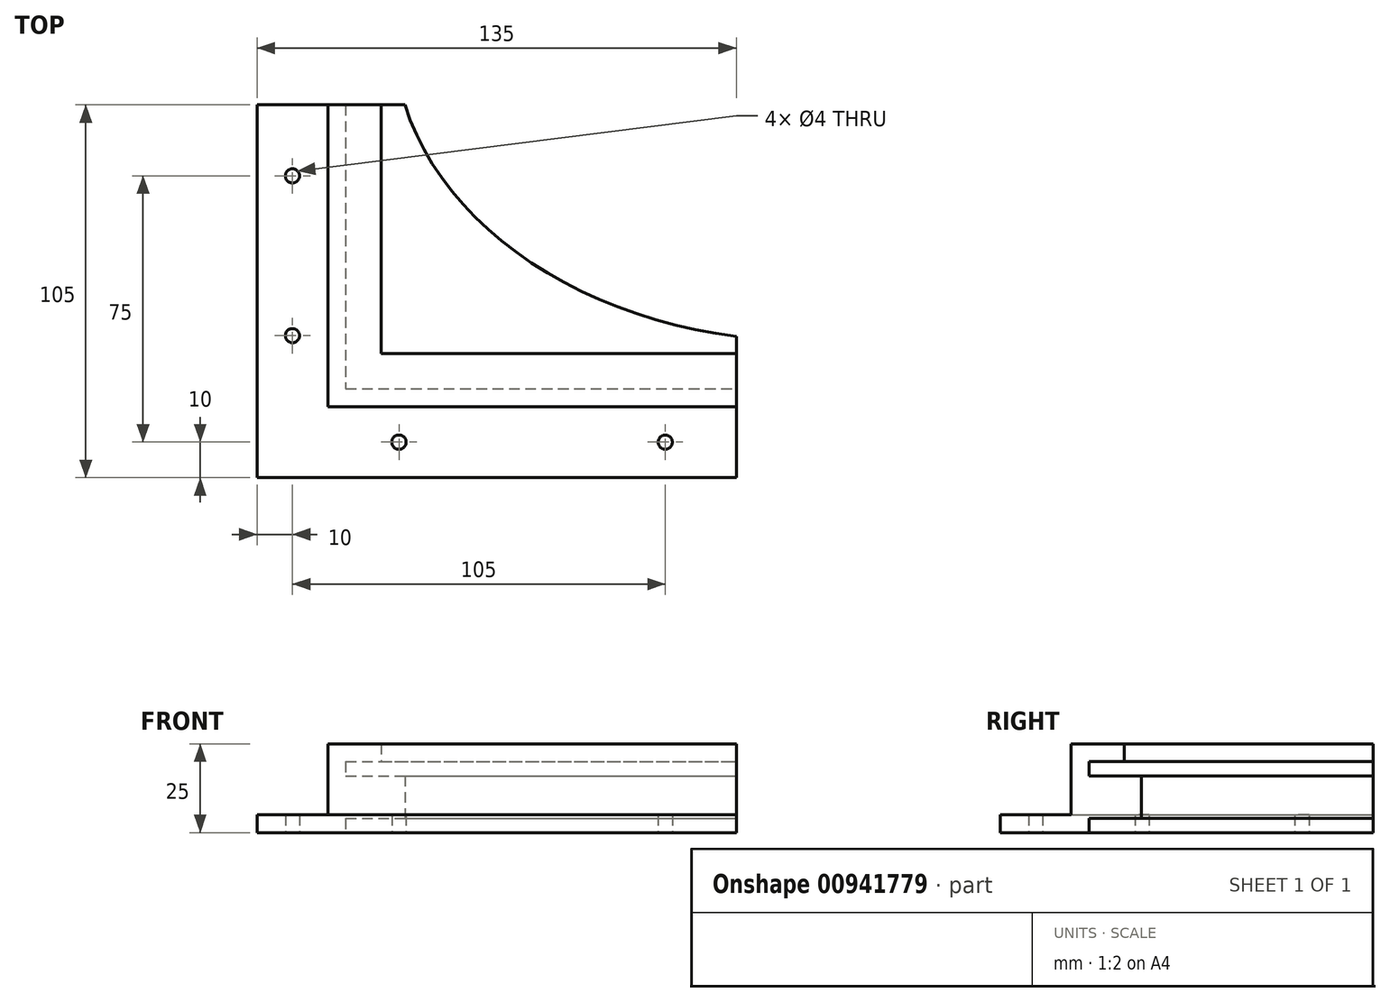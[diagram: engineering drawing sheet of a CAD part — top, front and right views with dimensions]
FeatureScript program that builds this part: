
annotation { "Feature Type Name" : "Feature", "Feature Type Description" : "" }
export const myFeature = defineFeature(function(context is Context, id is Id, definition is map)
    precondition{}
    {
        {
            var Q0;
            Q0=qCreatedBy(makeId("Top.planeOp"),FACE);
            var sketch = newSketch(context, id + "F0", { "sketchPlane" : qUnion([Q0])});
            skEllipticalArc(sketch, "E0", {});
            skLineSegment(sketch, "E1", {"start": v(-116.5, 0) * mm, "end": v(-116.5, -86.5) * mm});
            skPoint(sketch, "E1.endSnap0", {"position": v(0, -86.5) * mm});
            skLineSegment(sketch, "E2", {"start": v(-116.5, -86.5) * mm, "end": v(0, -86.5) * mm});
            skLineSegment(sketch, "E3", {"start": v(-116.5, 0) * mm, "end": v(-130, 0) * mm});
            skLineSegment(sketch, "E4", {"start": v(-130, 0) * mm, "end": v(-130, -100) * mm});
            skLineSegment(sketch, "E5", {"start": v(-130, -100) * mm, "end": v(0, -100) * mm});
            skLineSegment(sketch, "E6", {"start": v(0, -100) * mm, "end": v(0, -86.5) * mm});
            const initialGuessF0  = {"E0": [0, 0, 1, 0, 0.1165, 0.0865, 3.141592653589793, 4.71238898038469]};
            skSetInitialGuess(sketch, initialGuessF0);
            skSolve(sketch);
        }
        {
            var Q0;
            Q0=qSketchRegion(id+"F0",true);
            extrude(context, id + "F1", {"entities" : qUnion([Q0]), "depth" : 12 * mm, "offsetDistance" : 25 * mm});
        }
        {
            var Q0;
            Q0=makeQuery(id+"F1.opExtrude","SWEPT_FACE",FACE,{"disambiguationData":[OSD([sQuery(id+"F0.wireOp",EDGE,"E5")])]});
            var sketch = newSketch(context, id + "F2", { "sketchPlane" : qUnion([Q0])});
            skLineSegment(sketch, "E7.bottom", {"start": v(-130, 16) * mm, "end": v(0, 16) * mm});
            skLineSegment(sketch, "E7.top", {"start": v(-130, -4) * mm, "end": v(0, -4) * mm});
            skLineSegment(sketch, "E7.left", {"start": v(-130, 16) * mm, "end": v(-130, -4) * mm});
            skLineSegment(sketch, "E7.right", {"start": v(0, 16) * mm, "end": v(0, -4) * mm});
            skSolve(sketch);
        }
        {
            var Q0;
            Q0=qSketchRegion(id+"F2",true);
            extrude(context, id + "F3", {"entities" : qUnion([Q0]), "operationType" : NewBodyOperationType.ADD, "depth" : 5 * mm, "offsetDistance" : 25 * mm});
        }
        {
            var Q0;
            Q0=makeQuery(id+"F3.boolean.opBoolean","MERGE",FACE,{"derivedFrom":[makeQuery(id+"F1.opExtrude","SWEPT_FACE",FACE,{"disambiguationData":[OSD([sQuery(id+"F0.wireOp",EDGE,"E4")])]}),makeQuery(id+"F3.opExtrude","SWEPT_FACE",FACE,{"disambiguationData":[OSD([sQuery(id+"F2.wireOp",EDGE,"E7.left")])]})]});
            var sketch = newSketch(context, id + "F4", { "sketchPlane" : qUnion([Q0])});
            skLineSegment(sketch, "E8.bottom", {"start": v(105, 16) * mm, "end": v(0, 16) * mm});
            skLineSegment(sketch, "E8.top", {"start": v(105, -4) * mm, "end": v(0, -4) * mm});
            skLineSegment(sketch, "E8.left", {"start": v(105, 16) * mm, "end": v(105, -4) * mm});
            skLineSegment(sketch, "E8.right", {"start": v(0, 16) * mm, "end": v(0, -4) * mm});
            skSolve(sketch);
        }
        {
            var Q0;
            Q0=qSketchRegion(id+"F4",true);
            extrude(context, id + "F5", {"entities" : qUnion([Q0]), "operationType" : NewBodyOperationType.ADD, "depth" : 5 * mm, "offsetDistance" : 25 * mm});
        }
        {
            var Q0;
            Q0=makeQuery(id+"F5.boolean.opBoolean","MERGE",FACE,{"derivedFrom":[makeQuery(id+"F3.opExtrude","SWEPT_FACE",FACE,{"disambiguationData":[OSD([sQuery(id+"F2.wireOp",EDGE,"E7.top")])]}),makeQuery(id+"F5.opExtrude","SWEPT_FACE",FACE,{"disambiguationData":[OSD([sQuery(id+"F4.wireOp",EDGE,"E8.top")])]})]});
            var sketch = newSketch(context, id + "F6", { "sketchPlane" : qUnion([Q0])});
            skLineSegment(sketch, "E9", {"start": v(0, 125) * mm, "end": v(-155, 125) * mm});
            skLineSegment(sketch, "E10", {"start": v(-155, 125) * mm, "end": v(-155, 0) * mm});
            skLineSegment(sketch, "E11", {"start": v(-155, 0) * mm, "end": v(-135, 0) * mm});
            skLineSegment(sketch, "E12", {"start": v(-135, 0) * mm, "end": v(-135, 105) * mm});
            skLineSegment(sketch, "E13", {"start": v(-135, 105) * mm, "end": v(0, 105) * mm});
            skLineSegment(sketch, "E14", {"start": v(0, 105) * mm, "end": v(0, 125) * mm});
            skCircle(sketch, "E15", {"center": v(-145, 40) * mm, "radius": 2 * mm});
            skCircle(sketch, "E16", {"center": v(-145, 85) * mm, "radius": 2 * mm});
            skCircle(sketch, "E17", {"center": v(-115, 115) * mm, "radius": 2 * mm});
            skCircle(sketch, "E18", {"center": v(-40, 115) * mm, "radius": 2 * mm});
            skSolve(sketch);
        }
        {
            var Q0;
            Q0=qSketchRegion(id+"F6",true);
            extrude(context, id + "F7", {"entities" : qUnion([Q0]), "operationType" : NewBodyOperationType.ADD, "oppositeDirection" : true, "depth" : 5 * mm, "offsetDistance" : 25 * mm});
        }
        {
            var Q0;
            Q0=makeQuery(id+"F5.boolean.opBoolean","MERGE",FACE,{"derivedFrom":[makeQuery(id+"F3.opExtrude","SWEPT_FACE",FACE,{"disambiguationData":[OSD([sQuery(id+"F2.wireOp",EDGE,"E7.bottom")])]}),makeQuery(id+"F5.opExtrude","SWEPT_FACE",FACE,{"disambiguationData":[OSD([sQuery(id+"F4.wireOp",EDGE,"E8.bottom")])]})]});
            var sketch = newSketch(context, id + "F8", { "sketchPlane" : qUnion([Q0])});
            skLineSegment(sketch, "E19", {"start": v(-135, 0) * mm, "end": v(-120, 0) * mm});
            skLineSegment(sketch, "E20", {"start": v(-120, 0) * mm, "end": v(-120, -90) * mm});
            skLineSegment(sketch, "E21", {"start": v(-120, -90) * mm, "end": v(0, -90) * mm});
            skLineSegment(sketch, "E22", {"start": v(0, -90) * mm, "end": v(0, -105) * mm});
            skLineSegment(sketch, "E23", {"start": v(0, -105) * mm, "end": v(-135, -105) * mm});
            skLineSegment(sketch, "E24", {"start": v(-135, -105) * mm, "end": v(-135, 0) * mm});
            skSolve(sketch);
        }
        {
            var Q0;
            Q0=qSketchRegion(id+"F8",true);
            extrude(context, id + "F9", {"entities" : qUnion([Q0]), "operationType" : NewBodyOperationType.ADD, "depth" : 5 * mm, "offsetDistance" : 25 * mm});
        }
        {
            var Q0;
            Q0=qCreatedBy(makeId("Top.planeOp"),FACE);
            var sketch = newSketch(context, id + "F10", { "sketchPlane" : qUnion([Q0])});
            skLineSegment(sketch, "E25.bottom", {"start": v(-155, 0) * mm, "end": v(0, 0) * mm});
            skLineSegment(sketch, "E25.top", {"start": v(-155, -20) * mm, "end": v(0, -20) * mm});
            skLineSegment(sketch, "E25.left", {"start": v(-155, 0) * mm, "end": v(-155, -20) * mm});
            skLineSegment(sketch, "E25.right", {"start": v(0, 0) * mm, "end": v(0, -20) * mm});
            skLineSegment(sketch, "E26.bottom", {"start": v(0, -125) * mm, "end": v(-20, -125) * mm});
            skLineSegment(sketch, "E26.top", {"start": v(0, 0) * mm, "end": v(-20, 0) * mm});
            skLineSegment(sketch, "E26.left", {"start": v(0, -125) * mm, "end": v(0, 0) * mm});
            skLineSegment(sketch, "E26.right", {"start": v(-20, -125) * mm, "end": v(-20, 0) * mm});
            skSolve(sketch);
        }
        {
            var Q0;
            Q0=qSketchRegion(id+"F10",true);
            extrude(context, id + "F11", {"entities" : qUnion([Q0]), "operationType" : NewBodyOperationType.REMOVE, "endBound" : BoundingType.SYMMETRIC, "oppositeDirection" : true, "depth" : 50 * mm, "offsetDistance" : 25 * mm});
        }
    });
